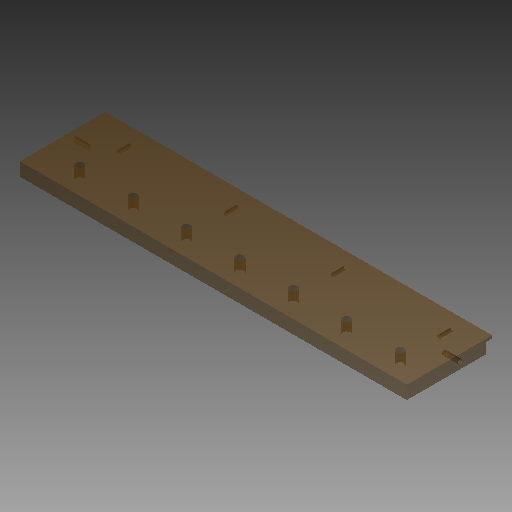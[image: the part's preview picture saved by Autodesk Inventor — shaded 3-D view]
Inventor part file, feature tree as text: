
AUTODESK INVENTOR PART (.ipt)
format: ipt  version: 2018 (Build 220112000, 112)  size: 126,464 bytes
history: native  units: mm
features: hole x3, extrude x2, pattern_linear x2, mirror x1, sketch x1
ambient origin geometry x8: Origin, YZ Plane, XZ Plane, XY Plane, X Axis, Y Axis, Z Axis, Center Point
bodies: Volumenkörper1 (feature_tree)
feature tree (9):
  extrude  "Extrusion1"  Depth=64.0mm
  extrude  "Extrusion2"  Depth=10.0mm TaperAngle=0.0deg
  hole  "Bohrung1"  [1 undecoded]
  pattern_linear  "Rechteckige Anordnung1"  Spacing1=5.0mm  [1 undecoded]
  hole  "Bohrung2"  [1 undecoded]
  pattern_linear  "Rechteckige Anordnung2"  Spacing1=25.0mm  [1 undecoded]
  hole  "Bohrung3"  [1 undecoded]
  mirror  "Spiegeln1"
  sketch  "Skizze5"  dims[d0=290.0mm d1=64.0mm d2=10.0mm d3=0.0mm d4=2.0mm d5=5.0mm d6=5.0mm d7=0.0mm d8=25.0mm d9=20.0mm d10=6.0mm d11=6.0mm d12=4.0mm d13=2.0mm d14=90.0deg d15=8.0mm d16=20.594885mm d17=70.0mm d19=40.0mm d20=25.0mm d21=4.0mm d22=2.459mm d23=8.0mm d24=4.0mm d25=2.0mm d26=90.0deg d27=10.0mm d28=20.594885mm d29=40.0mm d31=80.0mm d32=40.0mm d33=3.242mm d34=10.0mm d35=4.0mm d36=2.0mm d37=90.0deg d38=12.0mm d39=20.594885mm]
note: 5 required parameter values undecoded (feature->parameter linkage not recoverable at this tier; creation-order binding heuristic only, values carry confidence <= 0.55)
